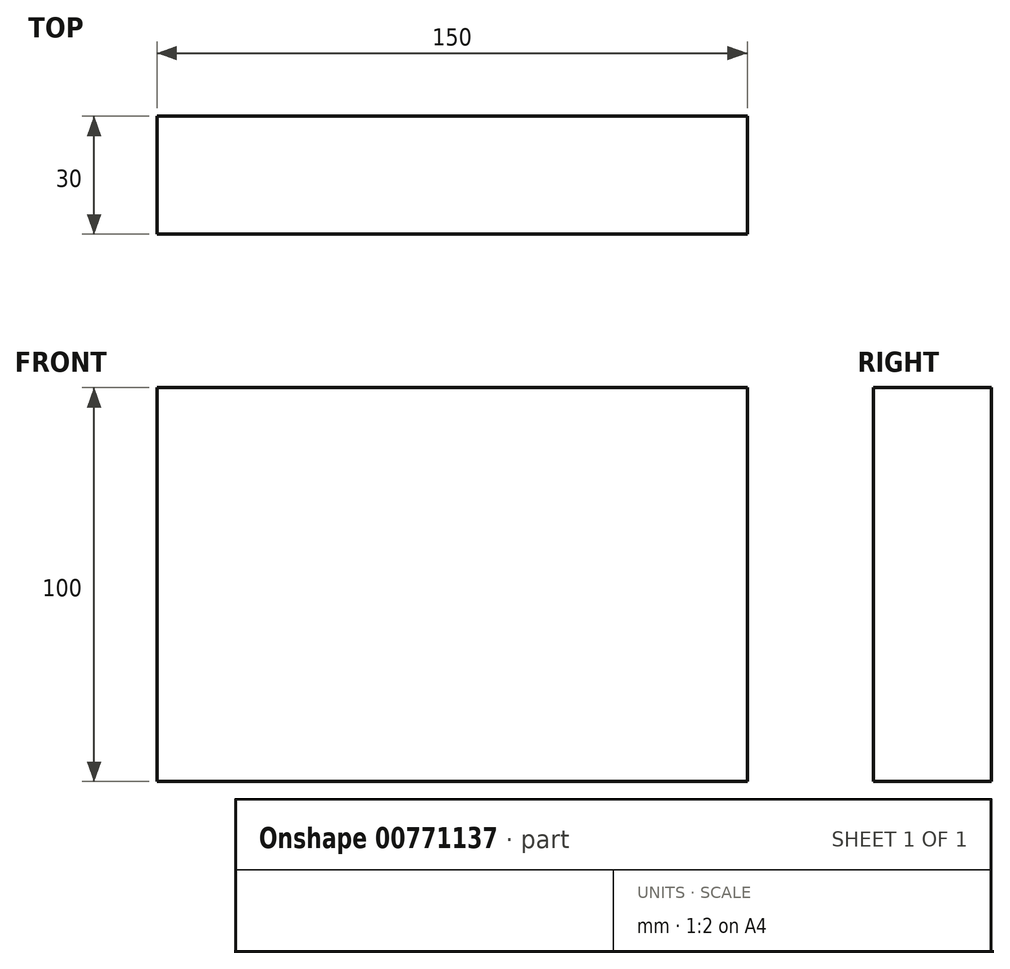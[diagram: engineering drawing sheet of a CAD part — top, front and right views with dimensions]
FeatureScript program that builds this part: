
annotation { "Feature Type Name" : "Feature", "Feature Type Description" : "" }
export const myFeature = defineFeature(function(context is Context, id is Id, definition is map)
    precondition{}
    {
        {
            var Q0;
            Q0=qCreatedBy(makeId("Front.planeOp"),FACE);
            var sketch = newSketch(context, id + "F0", { "sketchPlane" : qUnion([Q0])});
            skLineSegment(sketch, "E0.bottom", {"start": v(75, -50) * mm, "end": v(-75, -50) * mm});
            skLineSegment(sketch, "E0.top", {"start": v(75, 50) * mm, "end": v(-75, 50) * mm});
            skLineSegment(sketch, "E0.left", {"start": v(75, -50) * mm, "end": v(75, 50) * mm});
            skLineSegment(sketch, "E0.right", {"start": v(-75, -50) * mm, "end": v(-75, 50) * mm});
            skPoint(sketch, "E0.middle", {"position": v(0, 0) * mm});
            skSolve(sketch);
        }
        {
            var Q0;
            Q0 = qSketchRegion(id + "F0", true);
            extrude(context, id + "F1", {"entities" : qUnion([Q0]), "depth" : 30 * mm, "offsetDistance" : 25 * mm});
        }
    });
